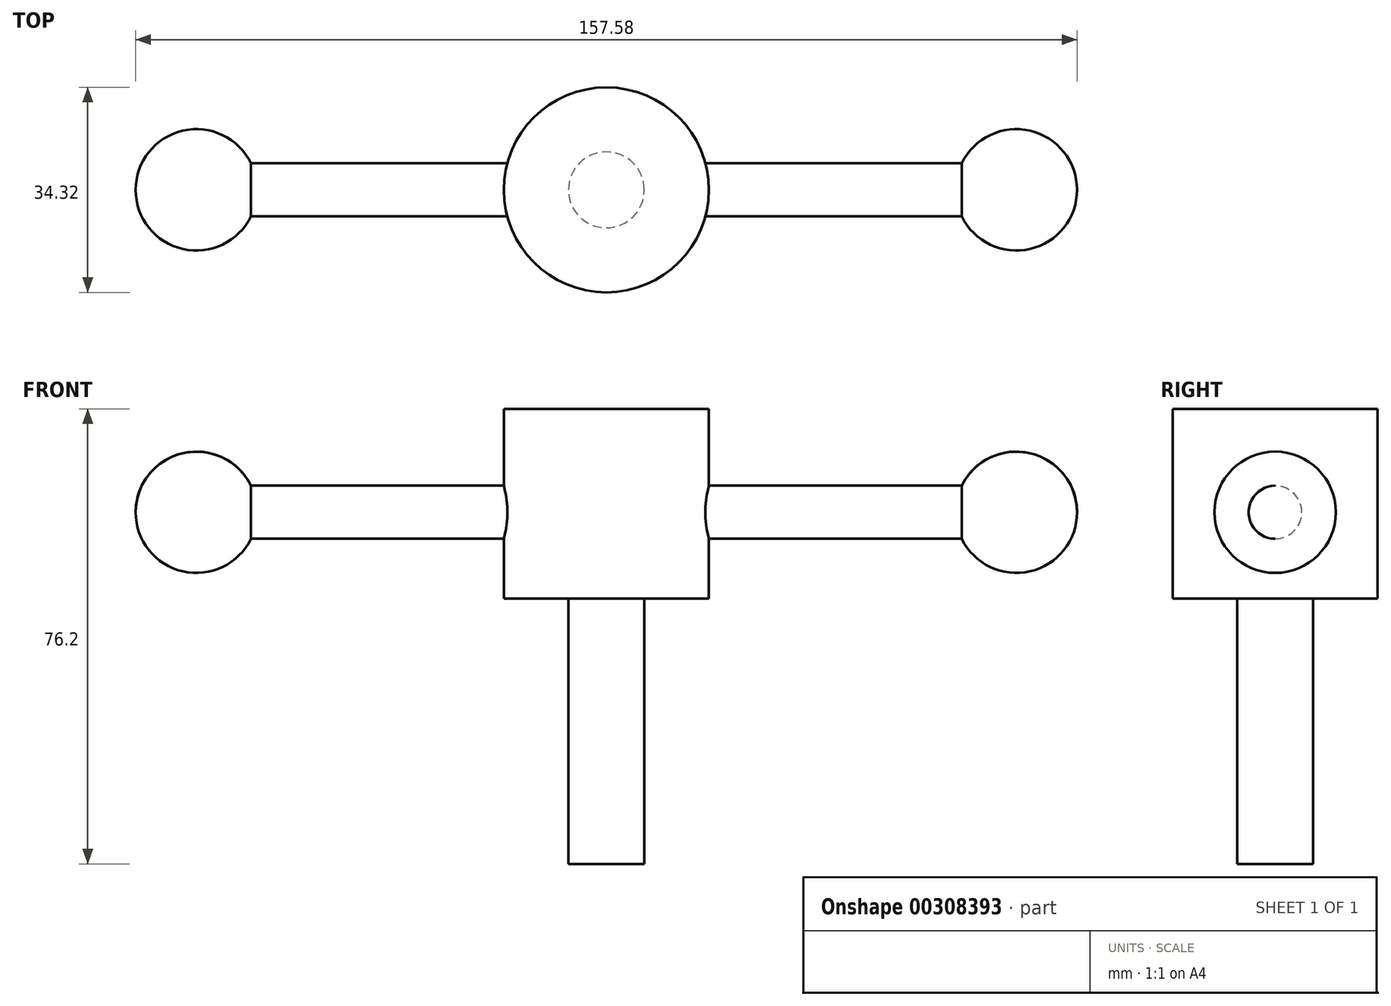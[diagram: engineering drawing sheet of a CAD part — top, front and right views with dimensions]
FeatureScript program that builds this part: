
annotation { "Feature Type Name" : "Feature", "Feature Type Description" : "" }
export const myFeature = defineFeature(function(context is Context, id is Id, definition is map)
    precondition{}
    {
        {
            var Q0;
            Q0=qCreatedBy(makeId("Front.planeOp"),FACE);
            var sketch = newSketch(context, id + "F0", { "sketchPlane" : qUnion([Q0])});
            skLineSegment(sketch, "E0", {"start": v(-77.72, 0) * mm, "end": v(112.04, 0) * mm, "construction": true});
            skLineSegment(sketch, "E1", {"start": v(0, 79.54) * mm, "end": v(0, -99.27) * mm, "construction": true});
            skLineSegment(sketch, "E2", {"start": v(17.16, 0) * mm, "end": v(17.16, 31.75) * mm});
            skLineSegment(sketch, "E3", {"start": v(17.16, 31.75) * mm, "end": v(0, 31.75) * mm});
            skLineSegment(sketch, "E4", {"start": v(-17.16, 0) * mm, "end": v(-58.56, 0) * mm});
            skLineSegment(sketch, "E5", {"start": v(-17.16, 0) * mm, "end": v(17.16, 0) * mm});
            skLineSegment(sketch, "E6", {"start": v(0, 31.75) * mm, "end": v(0, 0) * mm});
            skLineSegment(sketch, "E7", {"start": v(0, 0) * mm, "end": v(17.16, 0) * mm});
            skSolve(sketch);
        }
        {
            var Q0;
            Q0=makeQuery(id+"F0.imprint","IMPRINT",FACE,{"disambiguationData":[TD([[makeQuery(id+"F0.imprint","IMPRINT",EDGE,{"derivedFrom":sQuery(id+"F0.wireOp",EDGE,"E2")}),1.0]])]});
            var Q1;
            Q1=sQuery(id+"F0.wireOp",EDGE,"E1");
            revolve(context, id + "F1", {"entities" : qUnion([Q0]), "axis" : qUnion([Q1]), "revolveType" : RevolveType.FULL});
        }
        {
            var Q0;
            Q0=qCreatedBy(makeId("Front.planeOp"),FACE);
            var sketch = newSketch(context, id + "F2", { "sketchPlane" : qUnion([Q0])});
            skLineSegment(sketch, "E8", {"start": v(0, 0) * mm, "end": v(0, -66.7) * mm, "construction": true});
            skLineSegment(sketch, "E9", {"start": v(0, 0) * mm, "end": v(0, -44.45) * mm});
            skLineSegment(sketch, "E10", {"start": v(0, -44.45) * mm, "end": v(6.35, -44.45) * mm});
            skLineSegment(sketch, "E11", {"start": v(6.35, -44.45) * mm, "end": v(6.35, 0) * mm});
            skLineSegment(sketch, "E12", {"start": v(6.35, 0) * mm, "end": v(0, 0) * mm});
            skSolve(sketch);
        }
        {
            var Q0;
            Q0=makeQuery(id+"F2.imprint","IMPRINT",FACE,{"disambiguationData":[TD([[makeQuery(id+"F2.imprint","IMPRINT",EDGE,{"derivedFrom":sQuery(id+"F2.wireOp",EDGE,"E9")}),1.0]])]});
            var Q1;
            Q1=sQuery(id+"F2.wireOp",EDGE,"E8");
            revolve(context, id + "F3", {"operationType" : NewBodyOperationType.ADD, "entities" : qUnion([Q0]), "axis" : qUnion([Q1]), "revolveType" : RevolveType.FULL});
        }
        {
            var Q0;
            Q0=qCreatedBy(makeId("Front.planeOp"),FACE);
            var sketch = newSketch(context, id + "F4", { "sketchPlane" : qUnion([Q0])});
            skLineSegment(sketch, "E13", {"start": v(-7.7, 14.42) * mm, "end": v(-89.01, 14.42) * mm, "construction": true});
            skLineSegment(sketch, "E14", {"start": v(-7.7, 14.42) * mm, "end": v(-7.7, 18.87) * mm});
            skLineSegment(sketch, "E15", {"start": v(-7.7, 18.87) * mm, "end": v(-59.5, 18.87) * mm});
            skLineSegment(sketch, "E16", {"start": v(-58.47, 14.42) * mm, "end": v(-7.7, 14.42) * mm});
            skArc(sketch, "E17", {"start": v(-59.5, 18.87) * mm, "mid": v(-70.9, 24.32) * mm, "end": v(-78.79, 14.42) * mm});
            skLineSegment(sketch, "E18", {"start": v(-78.79, 14.42) * mm, "end": v(-58.47, 14.42) * mm});
            skLineSegment(sketch, "E19.MirrorCS", {"start": v(7.7, 18.87) * mm, "end": v(59.5, 18.87) * mm});
            skArc(sketch, "E20.MirrorCS", {"start": v(59.5, 18.87) * mm, "mid": v(70.9, 24.32) * mm, "end": v(78.79, 14.42) * mm});
            skLineSegment(sketch, "E21.MirrorCS", {"start": v(7.7, 14.42) * mm, "end": v(89.01, 14.42) * mm, "construction": true});
            skLineSegment(sketch, "E22", {"start": v(78.79, 14.42) * mm, "end": v(7.7, 14.42) * mm});
            skLineSegment(sketch, "E23", {"start": v(7.7, 14.42) * mm, "end": v(7.7, 18.87) * mm});
            skSolve(sketch);
        }
        {
            var Q0;
            Q0=makeQuery(id+"F4.imprint","IMPRINT",FACE,{"disambiguationData":[TD([[makeQuery(id+"F4.imprint","IMPRINT",EDGE,{"derivedFrom":sQuery(id+"F4.wireOp",EDGE,"E14")}),1.0]])]});
            var Q1;
            Q1=makeQuery(id+"F4.imprint","IMPRINT",FACE,{"disambiguationData":[TD([[makeQuery(id+"F4.imprint","IMPRINT",EDGE,{"derivedFrom":sQuery(id+"F4.wireOp",EDGE,"E19.MirrorCS")}),-1.0]])]});
            var Q2;
            Q2=sQuery(id+"F4.wireOp",EDGE,"E13");
            revolve(context, id + "F5", {"operationType" : NewBodyOperationType.ADD, "entities" : qUnion([Q0, Q1]), "axis" : qUnion([Q2]), "revolveType" : RevolveType.FULL});
        }
    });
